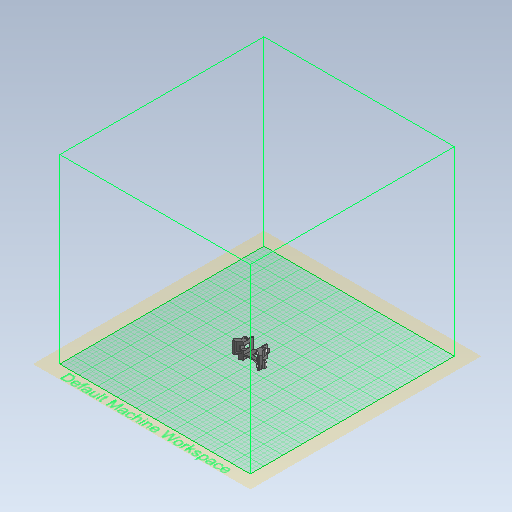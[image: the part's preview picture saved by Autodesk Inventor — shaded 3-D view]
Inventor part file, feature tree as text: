
AUTODESK INVENTOR PART (.ipt)
format: ipt  version: 2020 (Build 240168000, 168)  size: 1,733,632 bytes
history: native  units: mm
features: projected_geometry x61, extrude x30, sketch x30, other x11, chamfer x5, fillet x3, sweep x1
ambient origin geometry x8: Origin, YZ Plane, XZ Plane, XY Plane, X Axis, Y Axis, Z Axis, Center Point
bodies: Body1 (feature_tree)
feature tree (141):
  other  "Твердое тело1"
  extrude  "Выдавливание1"  Depth=35.0mm TaperAngle=0.0deg
  sketch  "Эскиз2"
  extrude  "Выдавливание2"  Depth=4.0mm
  sweep  "Сдвиг1"
  extrude  "Выдавливание5"  Depth=8.0mm
  extrude  "Выдавливание6"  Depth=35.0mm TaperAngle=0.0deg
  extrude  "Выдавливание7"  Depth=8.5mm
  extrude  "Выдавливание8"  TaperAngle=45.0deg  [1 undecoded]
  other  "РабПлоскость1"
  extrude  "Выдавливание9"  Depth=8.5mm
  extrude  "Выдавливание10"  TaperAngle=45.0deg  [1 undecoded]
  extrude  "Выдавливание11"  TaperAngle=0.0deg  [1 undecoded]
  sketch  "Эскиз13"
  other  "РабПлоскость2"
  sketch  "Эскиз14"
  extrude  "Выдавливание12"  Depth=5.0mm TaperAngle=0.0deg
  extrude  "Выдавливание13"  Depth=15.0mm TaperAngle=0.0deg
  other  "РабПлоскость3"
  extrude  "Выдавливание14"  Depth=15.0mm TaperAngle=0.0deg
  extrude  "Выдавливание15"  Depth=26.0mm
  extrude  "Выдавливание16"  Depth=6.0mm
  extrude  "Выдавливание17"  Depth=15.0mm TaperAngle=0.0deg
  chamfer  "Фаска1"  Distance=2.0mm
  other  "РабПлоскость4"
  sketch  "Эскиз18"
  extrude  "Выдавливание18"  Depth=1.5mm
  extrude  "Выдавливание19"  Depth=3.0mm
  extrude  "Выдавливание20"  Depth=6.0mm
  chamfer  "Фаска2"  Distance=2.5mm
  fillet  "Сопряжение1"  [1 undecoded]
  extrude  "Выдавливание21"  Depth=15.0mm TaperAngle=0.0deg
  extrude  "Выдавливание22"  Depth=10.0mm TaperAngle=0.0deg
  extrude  "Выдавливание23"  Depth=7.0mm TaperAngle=0.0deg
  other  "РабПлоскость5"
  extrude  "Выдавливание24"  Depth=40.0mm
  chamfer  "Фаска3"  Distance=3.8mm
  sketch  "Эскиз24"
  other  "РабПлоскость6"
  extrude  "Выдавливание25"  TaperAngle=0.0deg  [1 undecoded]
  sketch  "Эскиз26"
  other  "РабПлоскость7"
  sketch  "Эскиз27"
  extrude  "Выдавливание26"  Depth=16.5mm
  extrude  "Выдавливание27"  Depth=25.5mm
  extrude  "Выдавливание28"  Depth=2.3mm
  chamfer  "Фаска4"  Distance=3.0mm
  other  "РабПлоскость8"
  extrude  "Выдавливание29"  Depth=7.0mm
  other  "РабПлоскость9"
  extrude  "Выдавливание30"  Depth=18.0mm
  chamfer  "Фаска5"  Distance=1.5mm
  fillet  "Сопряжение2"  Radius=4.5mm
  fillet  "Сопряжение3"  Radius=6.5mm
  other  "РабПлоскость10"
  extrude  "Выдавливание31"  Depth=3.5mm
  extrude  "Выдавливание32"  Depth=1.0mm
  sketch  "Эскиз1"
  sketch  "Эскиз3"
  projected_geometry  "Спроецированная петля1"
  projected_geometry  "Спроецированная петля2"
  sketch  "3D эскиз1"
  sketch  "Эскиз4"
  sketch  "Эскиз6"
  projected_geometry  "Спроецированная петля4"
  sketch  "Эскиз7"
  projected_geometry  "Спроецированная петля5"
  sketch  "Эскиз9"
  projected_geometry  "Спроецированная петля7"
  sketch  "Эскиз11"
  projected_geometry  "Спроецированная петля8"
  sketch  "Эскиз12"
  projected_geometry  "Спроецированная петля9"
  projected_geometry  "Спроецированная петля10"
  sketch  "Эскиз15"
  sketch  "Эскиз16"
  projected_geometry  "Спроецированная петля11"
  projected_geometry  "Спроецированная петля12"
  sketch  "Эскиз17"
  projected_geometry  "Спроецированная петля13"
  projected_geometry  "Спроецированная петля14"
  projected_geometry  "Спроецированная петля15"
  projected_geometry  "Спроецированная петля16"
  sketch  "Эскиз19"
  projected_geometry  "Спроецированная петля17"
  sketch  "Эскиз20"
  projected_geometry  "Спроецированная петля18"
  projected_geometry  "Спроецированная петля19"
  projected_geometry  "Спроецированная петля20"
  projected_geometry  "Спроецированная петля21"
  projected_geometry  "Спроецированная петля22"
  projected_geometry  "Спроецированная петля23"
  sketch  "Эскиз21"
  projected_geometry  "Спроецированная петля24"
  projected_geometry  "Спроецированная петля25"
  projected_geometry  "Спроецированная петля26"
  projected_geometry  "Спроецированная петля27"
  projected_geometry  "Спроецированная петля28"
  projected_geometry  "Спроецированная петля29"
  projected_geometry  "Спроецированная петля30"
  projected_geometry  "Спроецированная петля31"
  sketch  "Эскиз22"
  projected_geometry  "Спроецированная петля32"
  projected_geometry  "Спроецированная петля33"
  sketch  "Эскиз23"
  projected_geometry  "Спроецированная петля34"
  projected_geometry  "Спроецированная петля35"
  projected_geometry  "Спроецированная петля36"
  projected_geometry  "Спроецированная петля37"
  sketch  "Эскиз25"
  projected_geometry  "Спроецированная петля38"
  projected_geometry  "Спроецированная петля39"
  projected_geometry  "Спроецированная петля40"
  projected_geometry  "Спроецированная петля41"
  projected_geometry  "Спроецированная петля42"
  projected_geometry  "Спроецированная петля43"
  projected_geometry  "Спроецированная петля44"
  projected_geometry  "Спроецированная петля45"
  projected_geometry  "Спроецированная петля46"
  projected_geometry  "Спроецированная петля47"
  projected_geometry  "Спроецированная петля48"
  projected_geometry  "Спроецированная петля49"
  sketch  "Эскиз28"
  projected_geometry  "Спроецированная петля50"
  projected_geometry  "Спроецированная петля51"
  projected_geometry  "Спроецированная петля52"
  projected_geometry  "Спроецированная петля53"
  projected_geometry  "Спроецированная петля54"
  sketch  "Эскиз29"
  sketch  "Эскиз30"
  projected_geometry  "Спроецированная петля55"
  projected_geometry  "Спроецированная петля56"
  sketch  "Эскиз31"
  projected_geometry  "Спроецированная петля57"
  sketch  "Эскиз32"
  projected_geometry  "Спроецированная петля58"
  projected_geometry  "Спроецированная петля59"
  projected_geometry  "Спроецированная петля60"
  projected_geometry  "Спроецированная петля61"
  projected_geometry  "Спроецированная петля62"
  projected_geometry  "Спроецированная петля63"
note: 5 required parameter values undecoded (feature->parameter linkage not recoverable at this tier; creation-order binding heuristic only, values carry confidence <= 0.55)
